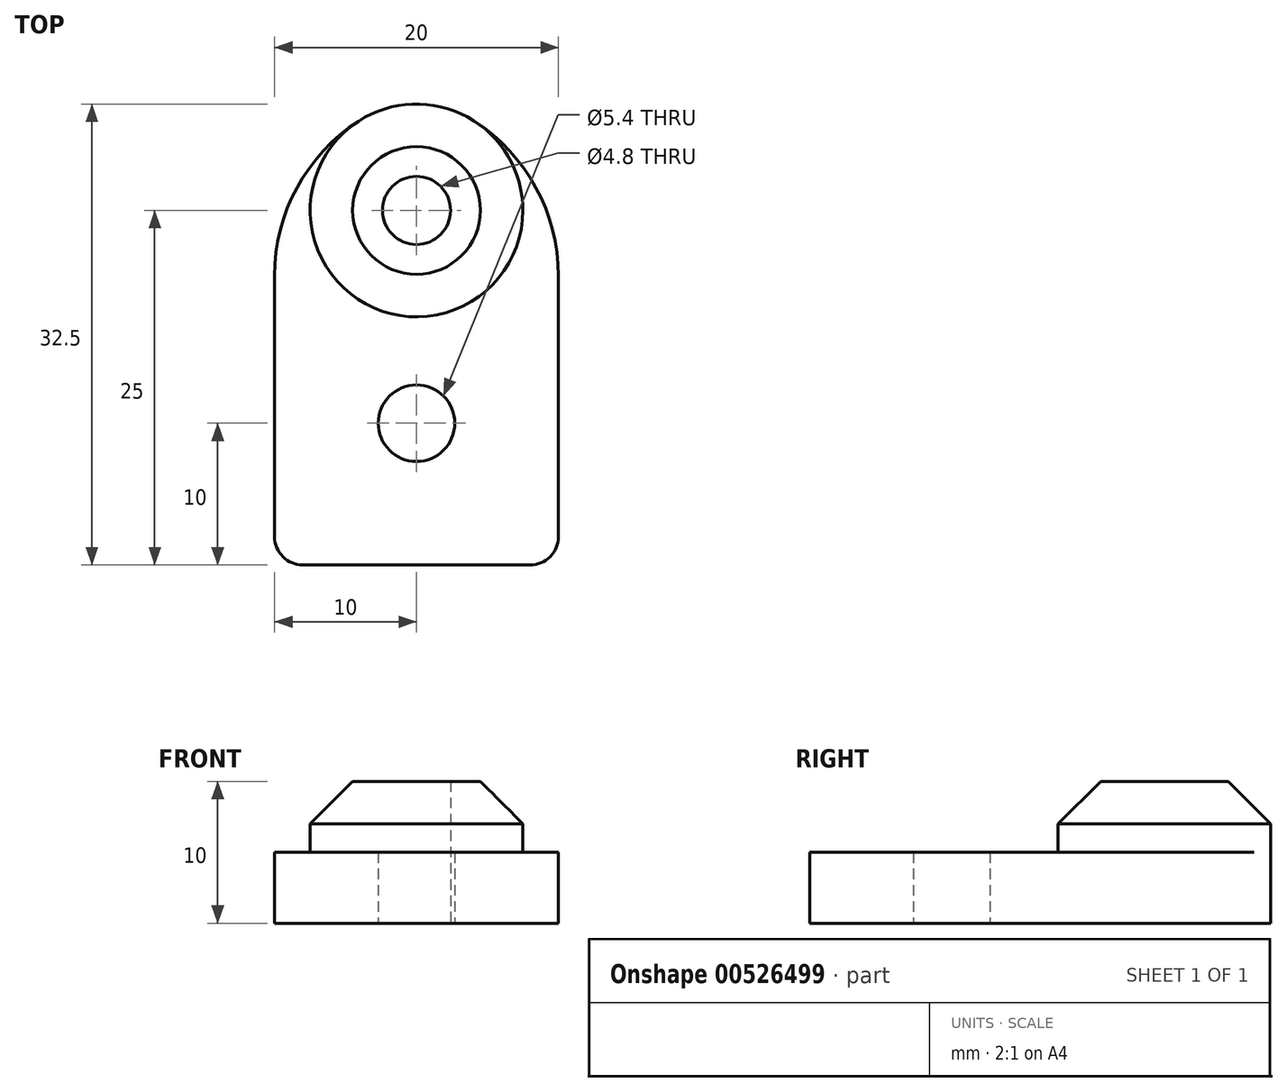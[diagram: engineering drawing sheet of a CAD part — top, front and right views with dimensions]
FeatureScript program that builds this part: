
annotation { "Feature Type Name" : "Feature", "Feature Type Description" : "" }
export const myFeature = defineFeature(function(context is Context, id is Id, definition is map)
    precondition{}
    {
        {
            var Q0;
            Q0=qCreatedBy(makeId("Top.planeOp"),FACE);
            var sketch = newSketch(context, id + "F0", { "sketchPlane" : qUnion([Q0])});
            skLineSegment(sketch, "E0", {"start": v(-10, 0) * mm, "end": v(10, 0) * mm});
            skLineSegment(sketch, "E1", {"start": v(10, 0) * mm, "end": v(10, 20.4) * mm});
            skLineSegment(sketch, "E2", {"start": v(-10, 20.4) * mm, "end": v(-10, 0) * mm});
            skArc(sketch, "E3", {"start": v(-10, 20.4) * mm, "mid": v(-8.42, 26.6) * mm, "end": v(-4.08, 31.3) * mm});
            skArc(sketch, "E4", {"start": v(-4.08, 31.3) * mm, "mid": v(0, 32.5) * mm, "end": v(4.08, 31.3) * mm});
            skArc(sketch, "E5", {"start": v(4.08, 31.3) * mm, "mid": v(8.42, 26.6) * mm, "end": v(10, 20.4) * mm});
            skCircle(sketch, "E6", {"center": v(0, 10) * mm, "radius": 2.7 * mm});
            skLineSegment(sketch, "E7", {"start": v(0, 10) * mm, "end": v(0, 0) * mm, "construction": true});
            skCircle(sketch, "E8", {"center": v(0, 25) * mm, "radius": 2.4 * mm});
            skSolve(sketch);
        }
        {
            var Q0;
            Q0=makeQuery(id+"F0.imprint","IMPRINT",FACE,{"disambiguationData":[TD([[makeQuery(id+"F0.imprint","IMPRINT",EDGE,{"derivedFrom":sQuery(id+"F0.wireOp",EDGE,"E0")}),1.0]])]});
            extrude(context, id + "F1", {"entities" : qUnion([Q0]), "depth" : 5 * mm, "offsetDistance" : 25 * mm});
        }
        {
            var Q0;
            Q0=makeQuery(id+"F1.opExtrude","CAP_FACE",FACE,{"disambiguationData":[OSD([sQuery(id+"F0.wireOp",EDGE,"E0"),sQuery(id+"F0.wireOp",EDGE,"E1"),sQuery(id+"F0.wireOp",EDGE,"E2"),sQuery(id+"F0.wireOp",EDGE,"E3"),sQuery(id+"F0.wireOp",EDGE,"E4"),sQuery(id+"F0.wireOp",EDGE,"E5"),sQuery(id+"F0.wireOp",EDGE,"E6"),sQuery(id+"F0.wireOp",EDGE,"E8")])],"isStart":false});
            var sketch = newSketch(context, id + "F2", { "sketchPlane" : qUnion([Q0])});
            skCircle(sketch, "E9", {"center": v(0, 25) * mm, "radius": 7.5 * mm});
            skCircle(sketch, "E10.0", {"center": v(0, 25) * mm, "radius": 2.4 * mm});
            skSolve(sketch);
        }
        {
            var Q0;
            Q0 = qSketchRegion(id + "F2", true);
            extrude(context, id + "F3", {"entities" : qUnion([Q0]), "operationType" : NewBodyOperationType.ADD, "depth" : 5 * mm, "offsetDistance" : 25 * mm});
        }
        {
            var Q0;
            Q0=makeQuery(id+"F3.opExtrude","CAP_EDGE",EDGE,{"disambiguationData":[OSD([sQuery(id+"F2.wireOp",EDGE,"E9")])],"isStart":false});
            chamfer(context, id + "F4", {"entities" : qUnion([Q0]), "width" : 3 * mm, "tangentPropagation" : true});
        }
        {
            var Q0;
            Q0=makeQuery(id+"F1.opExtrude","SWEPT_EDGE",EDGE,{"disambiguationData":[OSD([sQuery(id+"F0.wireOp",EDGE,"E0"),sQuery(id+"F0.wireOp",EDGE,"E2")])]});
            var Q1;
            Q1=makeQuery(id+"F1.opExtrude","SWEPT_EDGE",EDGE,{"disambiguationData":[OSD([sQuery(id+"F0.wireOp",EDGE,"E0"),sQuery(id+"F0.wireOp",EDGE,"E1")])]});
            fillet(context, id + "F5", {"entities" : qUnion([Q0, Q1]), "radius" : 2 * mm, "tangentPropagation" : true, "allowEdgeOverflow" : false});
        }
    });
